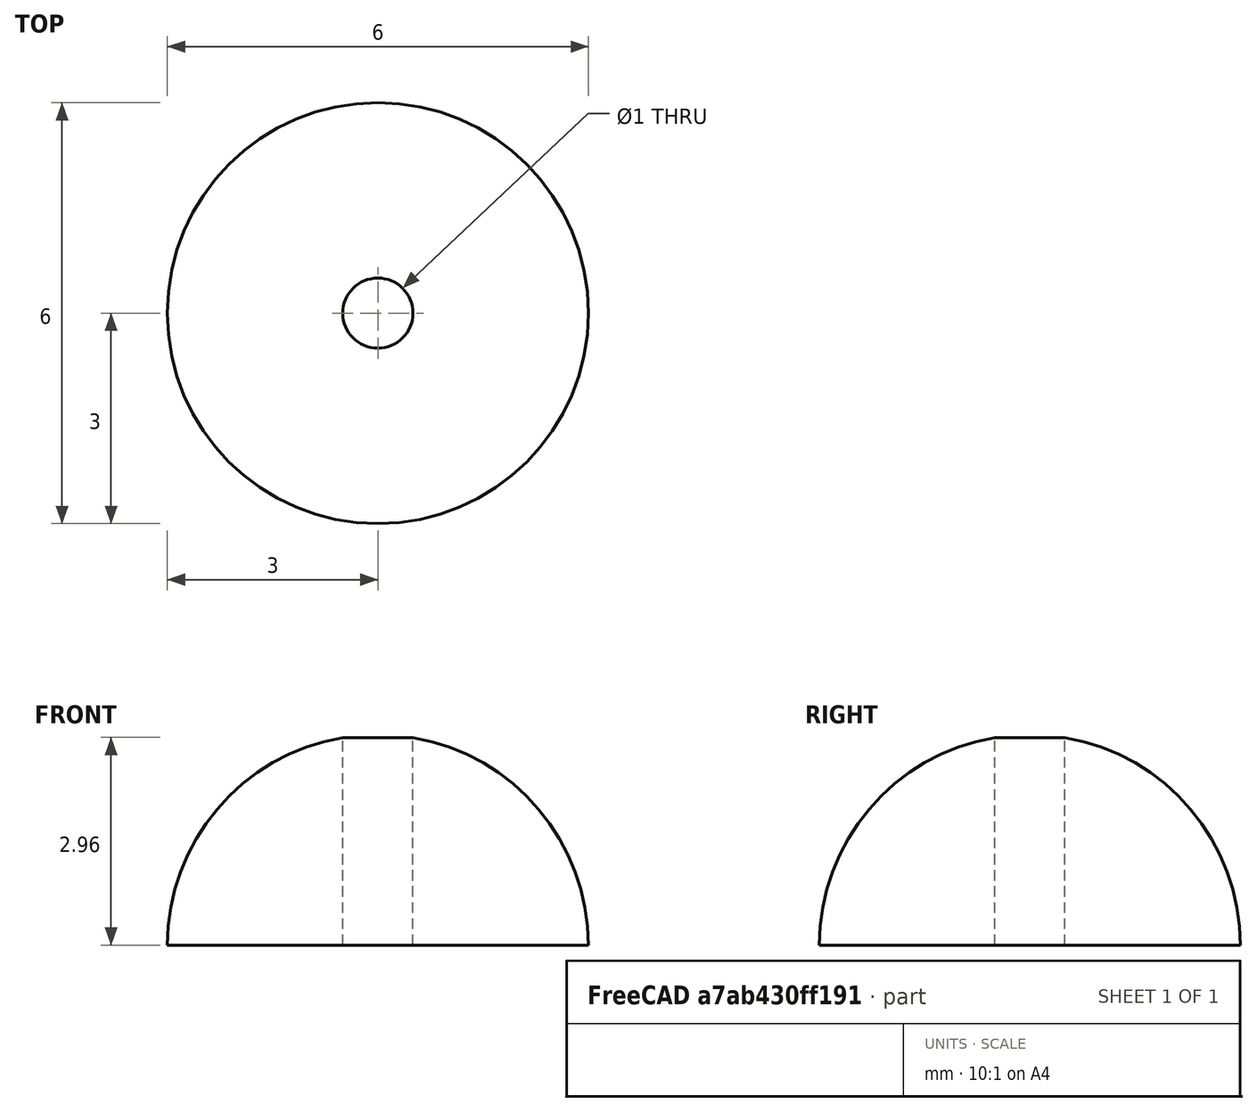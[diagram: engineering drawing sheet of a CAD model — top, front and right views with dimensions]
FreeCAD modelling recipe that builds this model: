
FCSTD DOCUMENT  (FreeCAD 1.1R39153 (Git))
Label: Полусфера
License: All rights reserved
LicenseURL: https://en.wikipedia.org/wiki/All_rights_reserved
objects: Sketcher::SketchObject×1, PartDesign::Revolution×1, PartDesign::Body×1
note: 6 computed .brp shape members not serialized (recipe doc carries the construction recipe); baked Part::Feature solids carry a one-line shape summary decoded from their .brp

FEATURE [Sketcher::SketchObject] Sketch
  ArcFitTolerance = 1e-06
  AttachmentSupport = -> [XZ_Plane]
  FullyConstrained = true
  MakeInternals = false
  MapMode = 5
  Placement = pos=(0,0,0) rot=(1,0,0;1.5708rad)
  sketch-geometry (3):
    g0: ArcOfCircle CenterX=0 CenterY=0 CenterZ=0 NormalX=0 NormalY=0 NormalZ=1 AngleXU=0 Radius=3 StartAngle=1.73824 EndAngle=3.14159
    g1: LineSegment StartX=-3 StartY=4e-16 StartZ=0 EndX=-0.5 EndY=4e-16 EndZ=0
    g2: LineSegment StartX=-0.5 StartY=4e-16 StartZ=0 EndX=-0.5 EndY=2.95804 EndZ=0
  constraints (9):
    c: Coincident(g0,g-1)
    c: PointOnObject(g0,g-1)
    c: Coincident(g1,g0)
    c: Horizontal(g1)
    c: Coincident(g2,g1)
    c: Vertical(g2)
    c: Coincident(g0,g2)
    c: DistanceX(g0,g-1) = 3
    c: DistanceX(g0,g0) = 0.5
FEATURE [PartDesign::Revolution] Revolution
  Angle = 360
  Angle2 = 60
  Axis = (0,2e-16,1)
  Base = (0,0,0)
  Placement = pos=(0,0,0) rot=(1,0,0;1.5708rad)
  Profile = -> Sketch
  ReferenceAxis = -> Sketch [V_Axis]
  Refine = true
  Suppressed = false
  Type = 0
FEATURE [PartDesign::Body] Body  label="Тело"
  AllowCompound = false
  Group = -> [Sketch,Revolution]
  Origin = -> Origin
  Tip = -> Revolution
